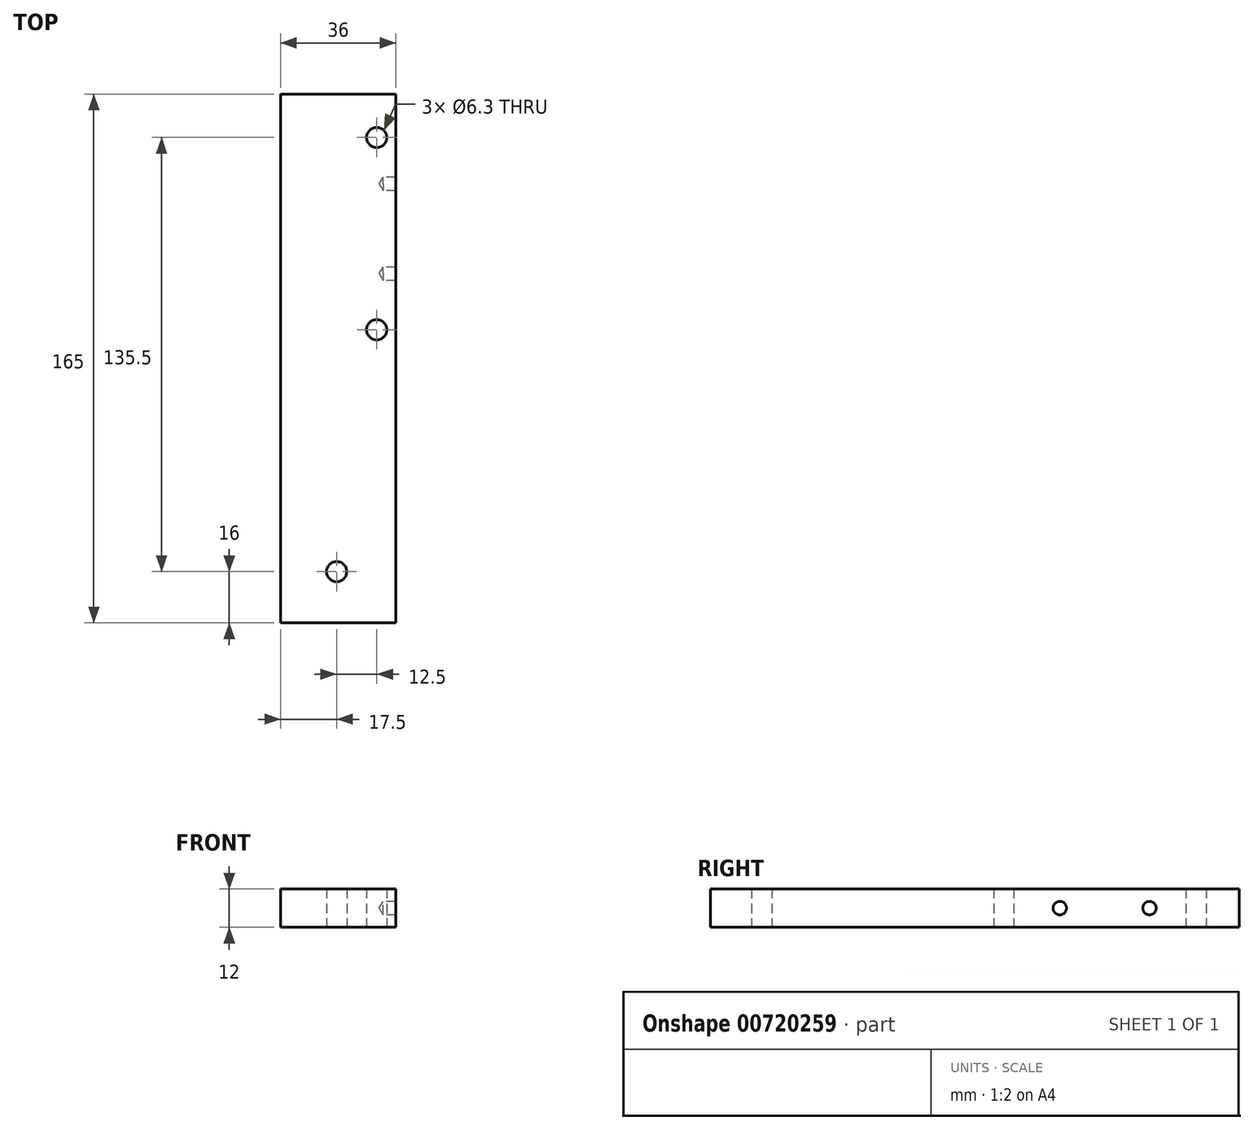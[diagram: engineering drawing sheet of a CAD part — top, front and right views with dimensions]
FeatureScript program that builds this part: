
annotation { "Feature Type Name" : "Feature", "Feature Type Description" : "" }
export const myFeature = defineFeature(function(context is Context, id is Id, definition is map)
    precondition{}
    {
        {
            var Q0;
            Q0=qCreatedBy(makeId("Top.planeOp"),FACE);
            var sketch = newSketch(context, id + "F0", { "sketchPlane" : qUnion([Q0])});
            skLineSegment(sketch, "E0.bottom", {"start": v(18, 82.5) * mm, "end": v(-18, 82.5) * mm});
            skLineSegment(sketch, "E0.top", {"start": v(18, -82.5) * mm, "end": v(-18, -82.5) * mm});
            skLineSegment(sketch, "E0.left", {"start": v(18, 82.5) * mm, "end": v(18, -82.5) * mm});
            skLineSegment(sketch, "E0.right", {"start": v(-18, 82.5) * mm, "end": v(-18, -82.5) * mm});
            skPoint(sketch, "E0.middle", {"position": v(0, 0) * mm});
            skSolve(sketch);
        }
        {
            var Q0;
            Q0=makeQuery(id+"F0.imprint","IMPRINT",FACE,{"disambiguationData":[TD([[makeQuery(id+"F0.imprint","IMPRINT",EDGE,{"derivedFrom":sQuery(id+"F0.wireOp",EDGE,"E0.bottom")}),1.0]])]});
            extrude(context, id + "F1", {"entities" : qUnion([Q0]), "depth" : 12 * mm, "offsetDistance" : 25 * mm});
        }
        {
            var Q0;
            Q0=makeQuery(id+"F1.opExtrude","CAP_FACE",FACE,{"disambiguationData":[OSD([sQuery(id+"F0.wireOp",EDGE,"E0.bottom"),sQuery(id+"F0.wireOp",EDGE,"E0.top"),sQuery(id+"F0.wireOp",EDGE,"E0.left"),sQuery(id+"F0.wireOp",EDGE,"E0.right")])],"isStart":false});
            var sketch = newSketch(context, id + "F2", { "sketchPlane" : qUnion([Q0])});
            skPoint(sketch, "E1", {"position": v(-0.5, -66.5) * mm});
            skPoint(sketch, "E2", {"position": v(12, 9) * mm});
            skPoint(sketch, "E3", {"position": v(12, 69) * mm});
            skSolve(sketch);
        }
        {
            var Q0;
            Q0=sQuery(id+"F2.wireOp",VERTEX,"E1");
            var Q1;
            Q1=sQuery(id+"F2.wireOp",VERTEX,"E2");
            var Q2;
            Q2=sQuery(id+"F2.wireOp",VERTEX,"E3");
            var Q3;
            Q3=makeQuery(id+"F1.opExtrude","SWEPT_BODY",BODY,{"disambiguationData":[OSD([sQuery(id+"F0.wireOp",EDGE,"E0.bottom"),sQuery(id+"F0.wireOp",EDGE,"E0.top"),sQuery(id+"F0.wireOp",EDGE,"E0.left"),sQuery(id+"F0.wireOp",EDGE,"E0.right")])]});
            hole(context, id + "F3", {"style" : HoleStyle.SIMPLE, "endStyle" : HoleEndStyle.BLIND, "standardTappedOrClearance" : lookupTablePath({ "standard" : "ISO", "fit" : "Close", "size" : "M6", "type" : "Clearance" }), "standardBlindInLast" : lookupTablePath({ "fit" : "Close", "standard" : "ISO", "size" : "M6", "type" : "Clearance" }), "holeDiameter" : 6.3 * mm, "majorDiameter" : 5 * mm, "holeDepth" : 40 * mm, "tappedDepth" : 12 * mm, "tapClearance" : 3, "locations" : qUnion([Q0, Q1, Q2]), "scope" : qUnion([Q3])});
        }
        {
            var Q0;
            Q0=makeQuery(id+"F1.opExtrude","SWEPT_FACE",FACE,{"disambiguationData":[OSD([sQuery(id+"F0.wireOp",EDGE,"E0.left")])]});
            var sketch = newSketch(context, id + "F4", { "sketchPlane" : qUnion([Q0])});
            skPoint(sketch, "E4", {"position": v(54.5, 6) * mm});
            skPoint(sketch, "E5", {"position": v(26.5, 6) * mm});
            skSolve(sketch);
        }
        {
            var Q0;
            Q0=sQuery(id+"F4.wireOp",VERTEX,"E5");
            var Q1;
            Q1=sQuery(id+"F4.wireOp",VERTEX,"E4");
            var Q2;
            Q2=makeQuery(id+"F1.opExtrude","SWEPT_BODY",BODY,{"disambiguationData":[OSD([sQuery(id+"F0.wireOp",EDGE,"E0.bottom"),sQuery(id+"F0.wireOp",EDGE,"E0.top"),sQuery(id+"F0.wireOp",EDGE,"E0.left"),sQuery(id+"F0.wireOp",EDGE,"E0.right")])]});
            hole(context, id + "F5", {"style" : HoleStyle.SIMPLE, "endStyle" : HoleEndStyle.BLIND, "standardTappedOrClearance" : lookupTablePath({ "standard" : "ISO", "fit" : "Close", "size" : "M4", "type" : "Clearance" }), "standardBlindInLast" : lookupTablePath({ "fit" : "Close", "standard" : "ISO", "size" : "M4", "type" : "Clearance" }), "holeDiameter" : 4.2 * mm, "majorDiameter" : 5 * mm, "holeDepth" : 4 * mm, "tappedDepth" : 12 * mm, "tapClearance" : 3, "locations" : qUnion([Q0, Q1]), "scope" : qUnion([Q2])});
        }
    });
